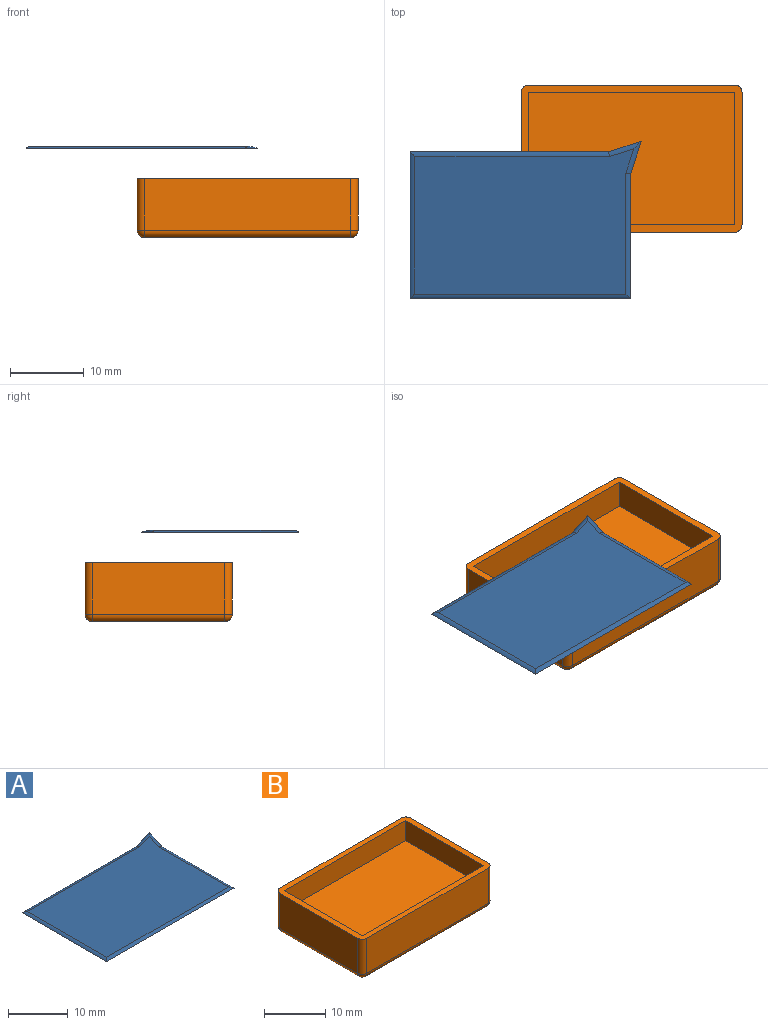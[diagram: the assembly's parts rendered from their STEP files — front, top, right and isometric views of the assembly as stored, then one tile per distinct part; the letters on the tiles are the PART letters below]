
ASSEMBLY  parts=2 mates=1
PART A: 8 faces, bbox 31.6x21.6x0.3 mm
  f0: plane 29.73x19.73mm, normal (0,0,1), area 538mm2, adj f2,f3,f4,f5,f6,f7
  f1: plane 31.41x21.41mm, normal (0,0,-1), area 604.2mm2, adj f2,f3,f4,f5,f6,f7
  f2: cylinder r=1mm len=30mm, axis (1,0,0), area 21.2mm2, adj f0,f1,f3,f4
  f3: cylinder r=1mm len=17.1mm, axis (0,1,0), area 12.1mm2, adj f0,f1,f2,f5
  f4: cylinder r=1mm len=20mm, axis (0,1,0), area 14mm2, adj f0,f1,f2,f6
  f5: cylinder r=1mm len=4.71mm, axis (-0.31,-0.95,0), area 2.9mm2, adj f0,f1,f3,f7
  f6: cylinder r=1mm len=27.1mm, axis (1,0,0), area 19.3mm2, adj f0,f1,f4,f7
  f7: cylinder r=1mm len=4.71mm, axis (-0.95,-0.31,0), area 2.9mm2, adj f0,f1,f5,f6
PART B: 23 faces, bbox 30x20x8 mm
  f0: plane 30x20mm, normal (0,0,1), area 95.1mm2, adj f1,f2,f3,f4,f6,f7,f8,f9
  f1: plane 18x7mm, normal (-1,0,0), area 126mm2, adj f0,f11,f14,f21
  f2: plane 28x7mm, normal (0,-1,0), area 196mm2, adj f0,f11,f12,f20
  f3: plane 18x7mm, normal (1,0,0), area 126mm2, adj f0,f12,f13,f16
  f4: plane 28x7mm, normal (0,1,0), area 196mm2, adj f0,f13,f14,f17
  f5: plane 28x18mm, normal (0,0,-1), area 504mm2, adj f16,f17,f20,f21
  f6: plane 28x4mm, normal (0,-1,0), area 112mm2, adj f0,f7,f9,f10
  f7: plane 18x4mm, normal (1,0,0), area 72mm2, adj f0,f6,f8,f10
  f8: plane 28x4mm, normal (0,1,0), area 112mm2, adj f0,f7,f9,f10
  f9: plane 18x4mm, normal (-1,0,0), area 72mm2, adj f0,f6,f8,f10
  f10: plane 28x18mm, normal (0,0,1), area 504mm2, adj f6,f7,f8,f9
  f11: cylinder r=1mm len=7mm, axis (0,0,1), area 11mm2, adj f0,f1,f2,f22
  f12: cylinder r=1mm len=7mm, axis (0,0,-1), area 11mm2, adj f0,f2,f3,f18
  f13: cylinder r=1mm len=7mm, axis (0,0,1), area 11mm2, adj f0,f3,f4,f15
  f14: cylinder r=1mm len=7mm, axis (0,0,-1), area 11mm2, adj f0,f1,f4,f19
  f15: sphere r=1mm, area 1.6mm2, adj f13,f16,f17
  f16: cylinder r=1mm len=18mm, axis (0,1,0), area 28.3mm2, adj f3,f5,f15,f18
  f17: cylinder r=1mm len=28mm, axis (-1,0,0), area 44mm2, adj f4,f5,f15,f19
  f18: sphere r=1mm, area 1.6mm2, adj f12,f16,f20
  f19: sphere r=1mm, area 1.6mm2, adj f14,f17,f21
  f20: cylinder r=1mm len=28mm, axis (1,0,0), area 44mm2, adj f2,f5,f18,f22
  f21: cylinder r=1mm len=18mm, axis (0,-1,0), area 28.3mm2, adj f1,f5,f19,f22
  f22: sphere r=1mm, area 1.6mm2, adj f11,f20,f21
PLACE A t=(-16.92,-9.01,12.12)mm
PLACE B t=(-1.82,0.06,0)mm fixed
MATE slider A.f1 <-> B.f0  axis (0,0,-1) through (-1.82,1.06,12.12)mm
